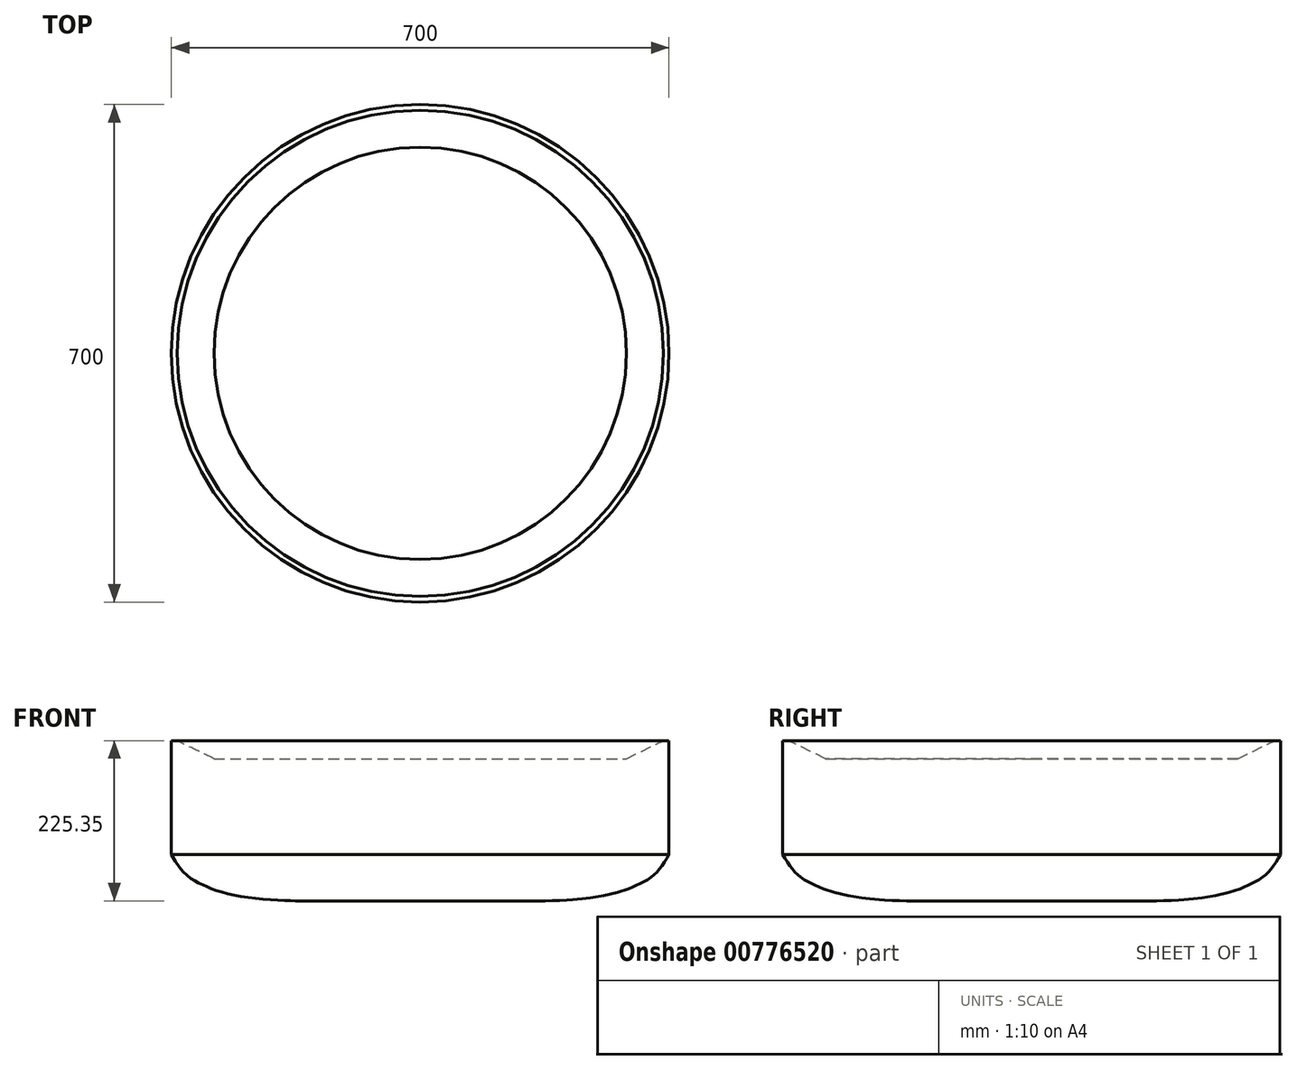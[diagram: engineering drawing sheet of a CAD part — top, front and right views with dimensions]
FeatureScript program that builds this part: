
annotation { "Feature Type Name" : "Feature", "Feature Type Description" : "" }
export const myFeature = defineFeature(function(context is Context, id is Id, definition is map)
    precondition{}
    {
        {
            var Q0;
            Q0=qCreatedBy(makeId("Front.planeOp"),FACE);
            var sketch = newSketch(context, id + "F0", { "sketchPlane" : qUnion([Q0])});
            skLineSegment(sketch, "E0", {"start": v(0, 0) * mm, "end": v(-290, 0) * mm});
            skLineSegment(sketch, "E1", {"start": v(-290, 0) * mm, "end": v(-342, 25.35) * mm});
            skLineSegment(sketch, "E2", {"start": v(-342, 25.35) * mm, "end": v(-350, 25.35) * mm});
            skLineSegment(sketch, "E3", {"start": v(-350, 25.35) * mm, "end": v(-350, -134.65) * mm});
            skFitSpline(sketch, "E4", {"points": [v(-350, -134.65) * mm, v(-310.55, -175.23) * mm, v(-260.72, -192.12) * mm, v(-175.42, -200) * mm], "startDerivative": vector(135.46, -251.6) * mm, "endDerivative": vector(148.58, 0) * mm});
            skLineSegment(sketch, "E5", {"start": v(-175.42, -200) * mm, "end": v(0, -200) * mm});
            skLineSegment(sketch, "E6", {"start": v(0, -200) * mm, "end": v(0, 0) * mm});
            skSolve(sketch);
        }
        {
            var Q0;
            Q0=makeQuery(id+"F0.imprint","IMPRINT",FACE,{"disambiguationData":[TD([[makeQuery(id+"F0.imprint","IMPRINT",EDGE,{"derivedFrom":sQuery(id+"F0.wireOp",EDGE,"E0")}),1.0]])]});
            var Q1;
            Q1=sQuery(id+"F0.wireOp",EDGE,"E6");
            revolve(context, id + "F1", {"surfaceOperationType" : NewSurfaceOperationType.NEW, "entities" : qUnion([Q0]), "axis" : qUnion([Q1]), "revolveType" : RevolveType.FULL});
        }
    });
